# Revit family: QF_ELECTROLUXPROFESSIONAL_1L0DEJ_TE1120P_E
name_source: partatom
category: Attrezzature speciali
units: mm (PartAtom-declared; Revit-internal decimal feet)

## family parameters
Basato su piano di lavoro = No
Condiviso = No
Punto di calcolo locali = No
Quota connettore circolare = Usa diametro
Sempre verticale = Sì
Taglio con vuoti quando caricato = No
Tipo di parte = Normale

## types (1)
- 916098136
    Cycle = 50 Hz
    Depth = 625 mm  [stored 2.05052 ft]
    Depth Actual = 625 mm  [stored 2.05052 ft]
    Descrizione = myPROzip SMART PROFESSIONAL TUMBLE DRYER TE1120P 8KG CONDENSE 220-240/50/1N 2,8KW SYMBOLS SCHUKO SST/DARK BLUE
    Gas KW = 0
    Height = 850 mm  [stored 2.78871 ft]
    Height Actual = 850 mm  [stored 2.78871 ft]
    Item Number = 1L0DFA
    Latent Heat Output = 0.0
    Length Actual = 596 mm
    Modello = TE1120P
    Phase = 1
    Produttore = Electrolux Professional
    Prospetto di default = 0 mm  [stored 0 ft]
    Sensible Heat Output = 0.0
    Steam Pounds per Hour = 0
    URL = www.electroluxprofessional.com
    Volts = 230 V
    Watts = 0 W
    Weight = 44
    Width = 597 mm

note: [stored X ft] marks values corroborated as IEEE doubles in the binary element streams (Revit-internal decimal feet)

## geometry (parser evidence)
native form markers: Sweep x2
no freeform markers — native parametric forms only
